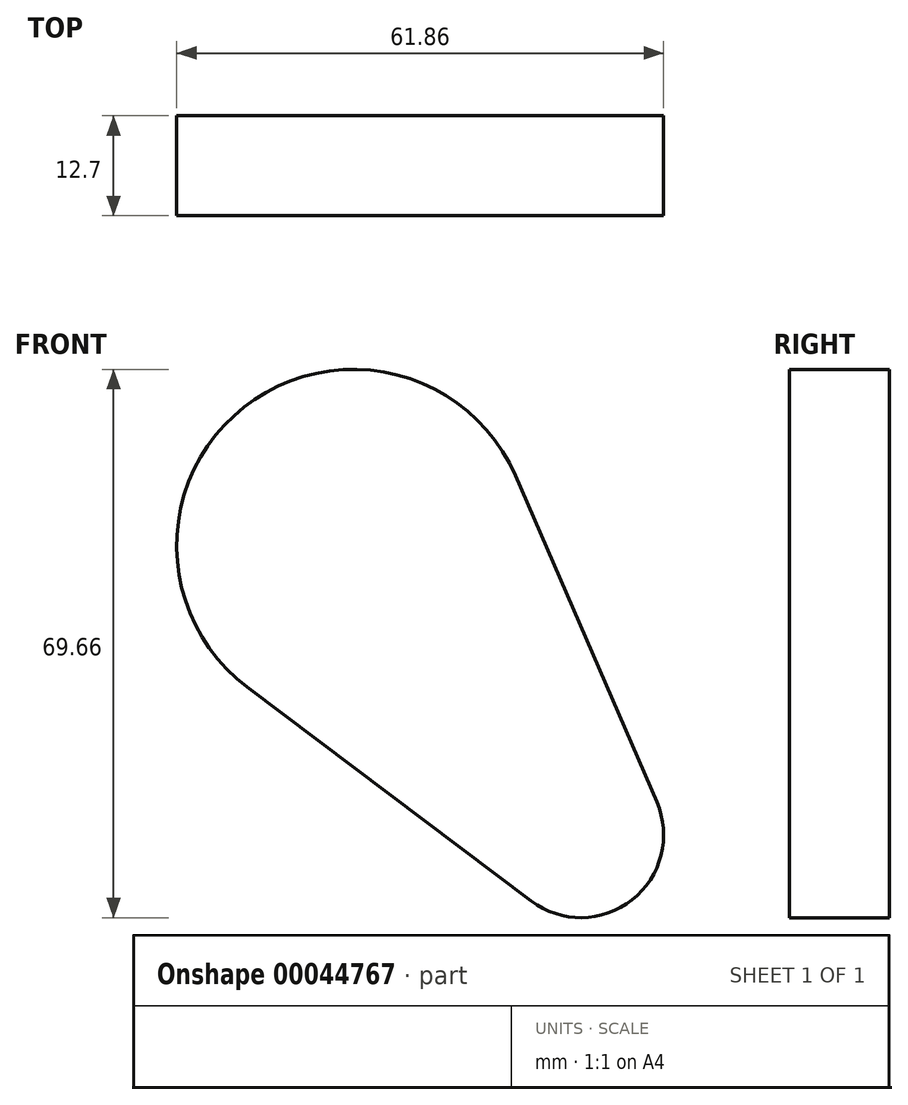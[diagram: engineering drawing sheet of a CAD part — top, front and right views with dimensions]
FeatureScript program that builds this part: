
annotation { "Feature Type Name" : "Feature", "Feature Type Description" : "" }
export const myFeature = defineFeature(function(context is Context, id is Id, definition is map)
    precondition{}
    {
        {
            var Q0;
            Q0=qCreatedBy(makeId("Front.planeOp"),FACE);
            var sketch = newSketch(context, id + "F0", { "sketchPlane" : qUnion([Q0])});
            skCircle(sketch, "E0", {"center": v(-3.5, 17.91) * mm, "radius": 22.43 * mm});
            skCircle(sketch, "E1", {"center": v(25.41, -18.8) * mm, "radius": 10.51 * mm});
            skLineSegment(sketch, "E2", {"start": v(-17, 0) * mm, "end": v(19.08, -27.2) * mm});
            skLineSegment(sketch, "E3", {"start": v(17.09, 26.84) * mm, "end": v(35.06, -14.61) * mm});
            skSolve(sketch);
        }
        {
            var Q0;
            Q0 = qSketchRegion(id + "F0", true);
            extrude(context, id + "F1", {"entities" : qUnion([Q0]), "depth" : 12.7 * mm});
        }
    });
